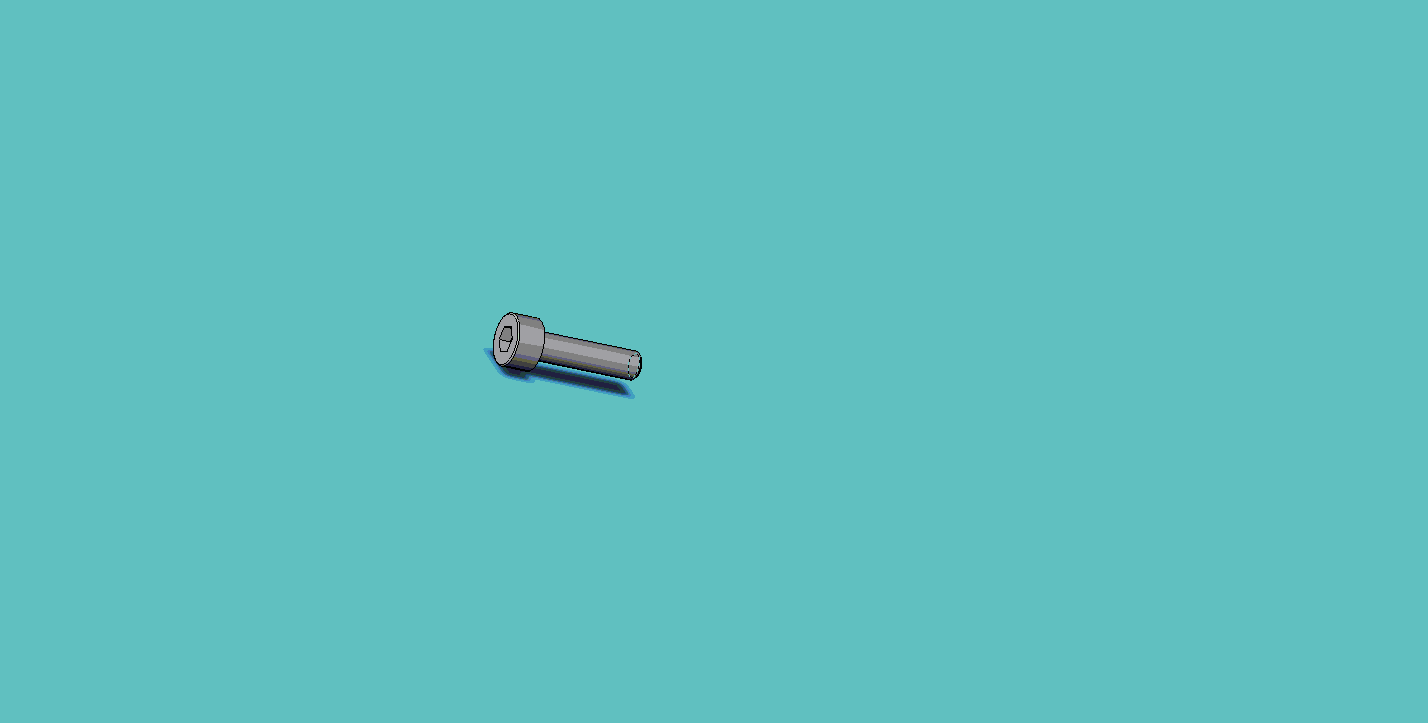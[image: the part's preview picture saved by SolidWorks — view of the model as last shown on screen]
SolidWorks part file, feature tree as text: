
SOLIDWORKS PART (.sldprt)
format: sldprt  version: not decoded by parser v0  size: 194,560 bytes
history: native  units: mm
features: sketch x4, plane x3, fillet x2, cut_revolve x2, material x1, revolve x1, thread x1, cut_extrude x1, pattern_linear x1 (+10 scaffold rows collapsed; 1 parser-record rows omitted)
feature tree (27):
  scaffold x10  (default folders/planes/origin — collapsed)
  material  "Material <not specified>"
  plane  "Plane1"
  plane  "Plane2"
  plane  "Plane3"
  parser-record x1  (decoder bookkeeping rows leaked as tree rows — omitted from the tree; the rows remain in map.json)
  revolve  "Base-Revolve"  [1 undecoded]
  sketch  "BodySke"  dims[c1.Head_fillet_rad=1.016mm c1.Head_top_radius=2.54mm c1.D1=19.05mm c1.Diameter=25.4mm c1.D3=50.8mm c1.D4=22.225mm c2.D4=45.0deg c2.D5=22.225mm c2.Head_ht=3.0mm c2.Length=12.0mm c2.D8=9.525mm c3.D8=45.0deg c3.D1=9.525mm c4.D8=9.525mm c5.D8=45.0deg c5.D1=73.025mm c6.D1=45.0deg c7.D1=9.525mm c8.D1=45.0deg c8.D4=22.225mm c9.D4=45.0deg c9.Thread_min=12.7mm c10.D4=9.525mm c10.Body_ch_ang=45.0deg c10.D8=22.225mm c11.D8=45.0deg c11.D5=22.225mm c12.D5=45.0deg c13.D5=~4.490128mm c14.D5=45.0deg c14.Head_dia=50.8mm c15.D5=~8.980256mm c15.Head_ch_ang=45.0deg c15.Head_side_ht=22.86mm c15.D9=19.05mm c15.Diameter=3.0mm c15.Head_dia=38.1mm c15.Minor_dia=2.439mm c15.Advance=0.5mm c15.Thread_nom=12.0mm c15.Thread_lim=~74.083342mm c15.Thread_length=60.0mm c16.Head_dia=5.5mm]
  thread  "ThreadCosmetic"  Diameter=10.5mm Thread_length=10.5mm Thread_minor=2.439mm  [1 undecoded]
  fillet  "Fillet1"  Radius=0.1mm Head_dia=5.5mm
  fillet  "Fillet2"  Radius=0.15mm
  sketch  "Sketch2"  dims[c1.D1=1.28mm c1.D2=25.4mm c2.D2=60.0deg c2.Wall_thickness=11.427mm c2.Depth=1.3mm]
  cut_revolve  "Hex-PreBroach"  Angle=360deg
  sketch  "Sketch3"  dims[c1.D1=1.28mm c1.D2=1.28mm c1.Hex_size=2.56mm c1.D4=~14.664697mm c2.D4=120.0deg]
  cut_extrude  "Hex"  Depth=1.3mm Key_eng=1.3mm
  sketch  "ThdSchSke"  dims[c1.Thread_minor=~1.03886mm c1.Diameter=~1.413535mm c1.Start=~0.988134mm c1.D4=~4.446753mm c1.Vee=60.0deg c2.Thread_minor=~1.03886mm c2.Start=~2.540025mm c2.D1=~0.108159mm c2.D2=~0.108159mm c3.D1=~0.216319mm c3.SideAngle=55.0deg c3.D2=~0.216319mm c3.VeeAngle=70.0deg c3.Thread_minor=2.439mm c3.Overcut=3.75mm c3.Diameter=3.0mm c3.D6=~8.326268mm c4.D1=~8.326268mm c5.D1=90.0deg c5.Start=54.0mm c6.Start=4.5mm]
  cut_revolve  "ThreadSchematic"  Angle=360deg
  pattern_linear  "ThdSchPat"  Count1=21 Count2=1 Spacing1=0.5mm Spacing2=50mm Num_threads=21 Advance=0.5mm CopiedFlag=1
decode coverage: 11 of 12 modeling features carry decoded parameters
note: ~ marks probable driven/reference dimensions
note: 2 parameter values undecoded
note: suppression state not decoded; provenance and decode notes live in map.json
